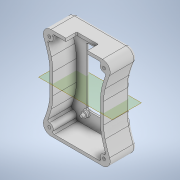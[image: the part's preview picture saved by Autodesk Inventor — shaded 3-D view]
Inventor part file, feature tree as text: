
AUTODESK INVENTOR PART (.ipt)
format: ipt  version: 2021 (Build 250183000, 183)  size: 387,072 bytes
history: native  units: mm
features: extrude x9, sketch x9, mirror x8, fillet x7, shell x1, plane x1
ambient origin geometry x8: Origin, YZ Plane, XZ Plane, XY Plane, X Axis, Y Axis, Z Axis, Center Point
bodies: Solid1 (feature_tree)
feature tree (35):
  extrude  "Extrusion1"  Depth=60.0mm
  extrude  "Extrusion2"  Depth=7.0mm
  mirror  "Mirror1"
  mirror  "Mirror2"
  fillet  "Fillet2"  Radius=20.0mm
  fillet  "Fillet3"  Radius=75.0mm
  shell  "Shell2"  Thickness=16.75mm
  extrude  "Extrusion3"  Depth=30.0mm
  fillet  "Fillet4"  Radius=5.0mm
  extrude  "Extrusion4"  Depth=2.0mm
  mirror  "Mirror4"
  mirror  "Mirror5"
  fillet  "Fillet5"  Radius=18.0mm
  plane  "Work Plane1"
  extrude  "Extrusion5"  Depth=1.0mm
  fillet  "Fillet6"  Radius=2.5mm
  mirror  "Mirror6"
  extrude  "Extrusion6"  Depth=5.0mm
  fillet  "Fillet7"  Radius=5.0mm
  mirror  "Mirror7"
  extrude  "Extrusion7"  Depth=1.0mm
  mirror  "Mirror8"
  extrude  "Extrusion8"  Depth=8.89mm
  mirror  "Mirror9"
  extrude  "Extrusion9"  Depth=0.5mm TaperAngle=0.0deg
  fillet  "Fillet8"  Radius=0.5mm
  sketch  "Sketch1"  dims[d0=35.0mm d1=60.0mm]
  sketch  "Sketch2"  dims[d2=17.25mm d3=0.0mm d5=7.0mm d7=20.0mm d8=75.0mm d9=16.75mm d10=0.0mm]
  sketch  "Sketch3"  dims[d12=2.0mm d13=30.0mm d14=5.0mm]
  sketch  "Sketch4"  dims[d15=2.0mm d16=38.0mm d17=18.0mm]
  sketch  "Sketch5"  dims[d18=0.0mm d19=0.0mm d20=1.0mm d21=2.5mm]
  sketch  "Sketch6"  dims[d22=1.0mm d23=1.9mm d24=5.0mm]
  sketch  "Sketch7"  dims[d25=0.0mm d26=0.0mm d27=1.0mm]
  sketch  "Sketch8"  dims[d28=20.86mm d29=8.89mm]
  sketch  "Sketch9"  dims[d30=3.6mm d31=1.5mm d32=0.0mm d33=0.5mm d34=24.86mm d35=8.89mm d36=1.5mm d37=0.0mm d38=0.5mm d39=1.75mm d40=2.0mm d41=0.0mm d42=1.9mm d43=2.0mm d44=0.0mm d45=7.0mm d46=14.0mm d47=2.0mm d48=0.0mm d49=0.5mm]
